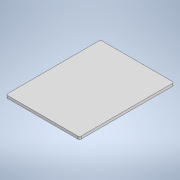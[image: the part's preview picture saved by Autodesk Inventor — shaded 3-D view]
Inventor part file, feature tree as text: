
AUTODESK INVENTOR PART (.ipt)
format: ipt  version: 2022 (Build 260153000, 153)  size: 106,496 bytes
history: native  units: in
note: dims shown in document units (in); Inventor stores cm internally (conversion verified against a paired STEP export)
features: fillet x4, extrude x1, sketch x1
ambient origin geometry x8: Origin, YZ Plane, XZ Plane, XY Plane, X Axis, Y Axis, Z Axis, Center Point
bodies: Solid1 (feature_tree)
feature tree (6):
  extrude  "Extrusion1"  Depth=7.0866in
  fillet  "Face Fillet1"
  fillet  "Face Fillet2"
  fillet  "Face Fillet3"
  fillet  "Face Fillet4"
  sketch  "Sketch1"  dims[d0=5.5118in d1=7.0866in d2=0.1969in d3=0.0in d4=0.1181in d5=0.1181in d6=0.1181in d7=0.1181in]
